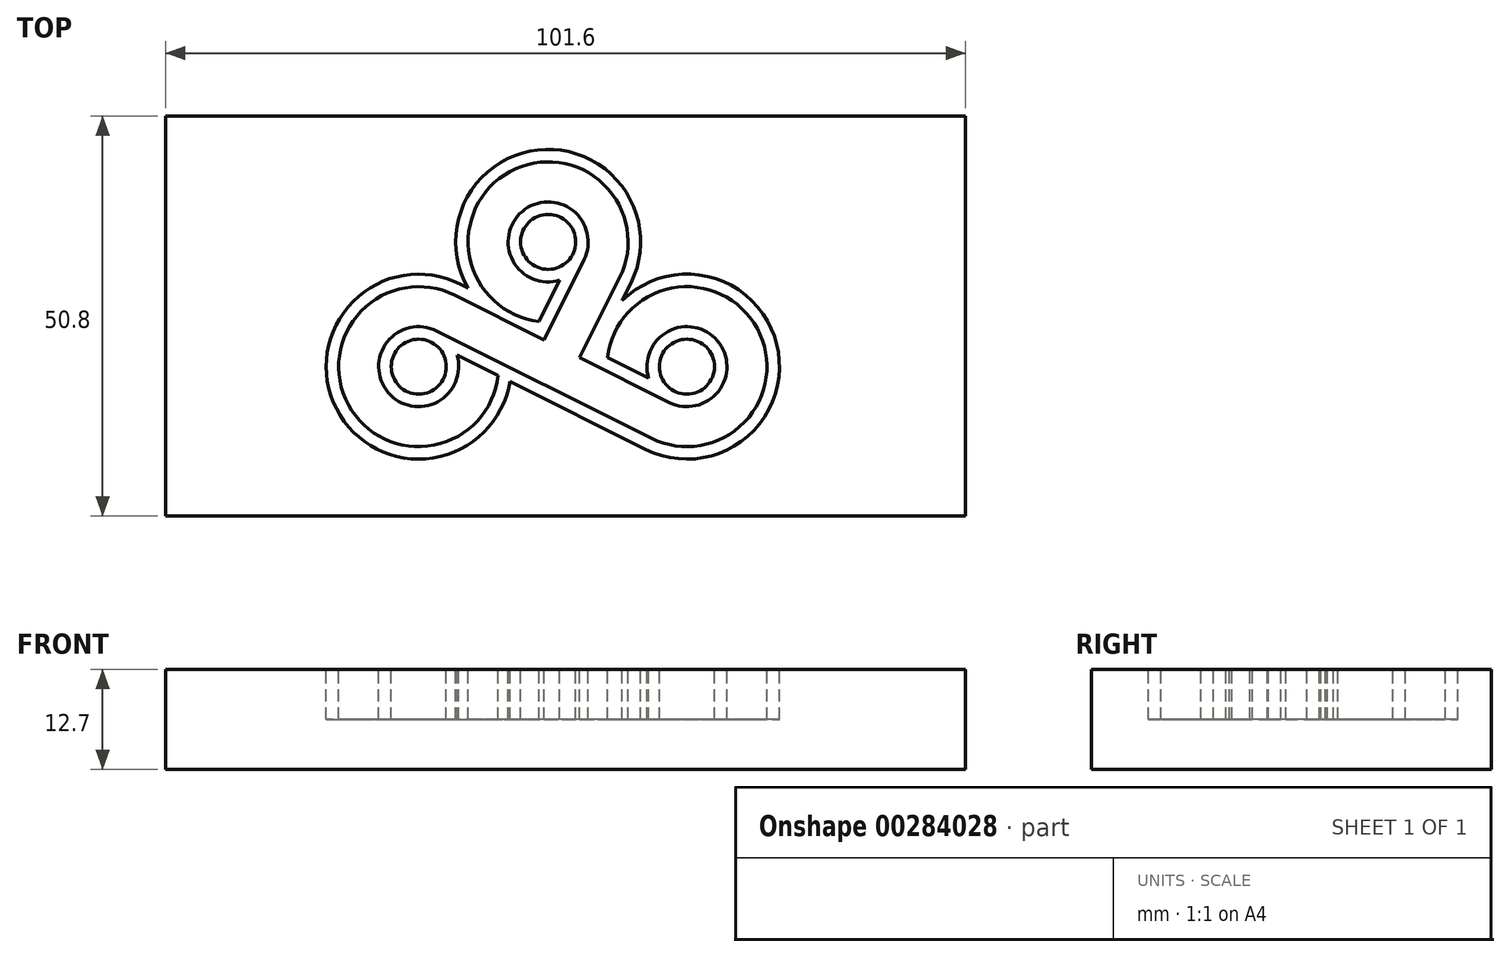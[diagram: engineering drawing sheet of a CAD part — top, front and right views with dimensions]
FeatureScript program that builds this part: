
annotation { "Feature Type Name" : "Feature", "Feature Type Description" : "" }
export const myFeature = defineFeature(function(context is Context, id is Id, definition is map)
    precondition{}
    {
        {
            var Q0;
            Q0=qCreatedBy(makeId("Top.planeOp"),FACE);
            var sketch = newSketch(context, id + "F0", { "sketchPlane" : qUnion([Q0])});
            skLineSegment(sketch, "E0.bottom", {"start": v(-49.28, -25.2) * mm, "end": v(52.32, -25.2) * mm});
            skLineSegment(sketch, "E0.top", {"start": v(-49.28, 25.6) * mm, "end": v(52.32, 25.6) * mm});
            skLineSegment(sketch, "E0.left", {"start": v(-49.28, -25.2) * mm, "end": v(-49.28, 25.6) * mm});
            skLineSegment(sketch, "E0.right", {"start": v(52.32, -25.2) * mm, "end": v(52.32, 25.6) * mm});
            skSolve(sketch);
        }
        {
            var Q0;
            Q0 = qSketchRegion(id + "F0", true);
            extrude(context, id + "F1", {"entities" : qUnion([Q0]), "oppositeDirection" : true, "depth" : 12.7 * mm});
        }
        {
            var Q0;
            Q0=qCreatedBy(makeId("Top.planeOp"),FACE);
            var sketch = newSketch(context, id + "F2", { "sketchPlane" : qUnion([Q0])});
            skLineSegment(sketch, "E1", {"start": v(-14.86, -1.7) * mm, "end": v(12.4, -15.33) * mm});
            skLineSegment(sketch, "E2", {"start": v(-12.6, 2.85) * mm, "end": v(-1.23, -2.83) * mm});
            skLineSegment(sketch, "E3", {"start": v(-1.23, -2.83) * mm, "end": v(3.85, 7.34) * mm});
            skLineSegment(sketch, "E4", {"start": v(3.3, -5.1) * mm, "end": v(14.67, -10.78) * mm});
            skArc(sketch, "E5", {"start": v(-12.6, 2.85) * mm, "mid": v(-26.07, -11.09) * mm, "end": v(-7.04, -7.38) * mm});
            skArc(sketch, "E6", {"start": v(12.4, -15.33) * mm, "mid": v(25.87, -1.4) * mm, "end": v(6.85, -5.1) * mm});
            skArc(sketch, "E7", {"start": v(8.4, 5.06) * mm, "mid": v(-5.54, 18.54) * mm, "end": v(-1.84, -0.49) * mm});
            skArc(sketch, "E8", {"start": v(-14.86, -1.7) * mm, "mid": v(-21.02, -9.52) * mm, "end": v(-12.28, -4.77) * mm});
            skArc(sketch, "E9", {"start": v(14.67, -10.78) * mm, "mid": v(20.82, -2.96) * mm, "end": v(12.08, -7.71) * mm});
            skArc(sketch, "E10", {"start": v(3.85, 7.34) * mm, "mid": v(-3.97, 13.5) * mm, "end": v(0.78, 4.75) * mm});
            skLineSegment(sketch, "E11", {"start": v(-12.28, -4.77) * mm, "end": v(-7.04, -7.38) * mm});
            skLineSegment(sketch, "E12", {"start": v(0.78, 4.75) * mm, "end": v(-1.84, -0.49) * mm});
            skLineSegment(sketch, "E13", {"start": v(6.85, -5.1) * mm, "end": v(12.08, -7.71) * mm});
            skLineSegment(sketch, "E14", {"start": v(8.4, 5.06) * mm, "end": v(3.3, -5.1) * mm});
            skCircle(sketch, "E15", {"center": v(-0.7, 9.6) * mm, "radius": 3.5 * mm});
            skCircle(sketch, "E16", {"center": v(-17.14, -6.24) * mm, "radius": 3.5 * mm});
            skCircle(sketch, "E17", {"center": v(16.94, -6.24) * mm, "radius": 3.5 * mm});
            skArc(sketch, "E18", {"start": v(9.81, 4.35) * mm, "mid": v(-1.03, 21.35) * mm, "end": v(-10.89, 3.77) * mm});
            skArc(sketch, "E19", {"start": v(-11.88, 4.27) * mm, "mid": v(-27.6, -11.59) * mm, "end": v(-5.54, -8.13) * mm});
            skLineSegment(sketch, "E20", {"start": v(-11.88, 4.27) * mm, "end": v(-10.89, 3.77) * mm});
            skArc(sketch, "E21", {"start": v(11.69, -16.75) * mm, "mid": v(28.54, -4.4) * mm, "end": v(8.7, 2.14) * mm});
            skLineSegment(sketch, "E22", {"start": v(9.81, 4.35) * mm, "end": v(8.7, 2.14) * mm});
            skLineSegment(sketch, "E23", {"start": v(-5.54, -8.13) * mm, "end": v(11.69, -16.75) * mm});
            skSolve(sketch);
        }
        {
            var Q0;
            Q0 = qSketchRegion(id + "F2", true);
            extrude(context, id + "F3", {"entities" : qUnion([Q0]), "operationType" : NewBodyOperationType.REMOVE, "oppositeDirection" : true, "depth" : 6.35 * mm});
        }
    });
